# Revit family: Electronics_Visual-TVs_ViewSonic_ViewSonicR-EP4320-5540-5540T-Display
name_source: partatom
category: Electrical Equipment
revit_build: Autodesk Revit 2017 (Build: 20190508_0315(x64)
units: mm (PartAtom-declared; Revit-internal decimal feet)

## family parameters
Always vertical = Yes
Cut with Voids When Loaded = No
OmniClass Number = 23.85.10.14.24.17
OmniClass Title = Plasma Video Monitors
Panel Configuration = Two Columns, Circuits Across
Part Type = Panelboard
Room Calculation Point = No
Round Connector Dimension = Use Diameter
Shared = No
Work Plane-Based = No

## types (3) — shared parameters
Aspect Ratio = 9:16
Assembly Code = D5030500
Backlight = WLED
Contrast Ratio = 1200:1
Cover Material = Plastic - Screen - ViewSonic
Covering Color = Metal - ViewSonic - Black
Edition number = 1
Keynote = 11130
Light Source = DLED
Manufacturer = ViewSonic
Orientation = Portrait
Panel Surface = 7H/ 5mm Tempered glass
Product data url = https://www.bimobject.com
URL = https://www.viewsonic.com
Viewing Angles = H = 178, V = 178 typ.

## per-type parameters (varying)
| type | Backlight Life | Brightness | Colors | Description | Display Area | Display Size | EP4320 | EP5540 | EP5540T | Model | Panel Size | Product Guid | Resolution | Response Time | Screen Material | Surface Treatment | Type/Tech | Viewable Area (In.) |
| EP 4320 | 50,000 hrs | 450 cd/m2 | 16.7M colors | The ViewSonic® EP4320-2 is a 43” all-in-one free-standing digital ePoster kiosk with a sleek, slim design. Great for grabbing attention in busy, high-traffic areas, the EP4320-2 comes with a scratch-proof tempered glass faceplate for added durability. Featuring Full HD 1080p resolution, 178°/178° wide-angle viewing, 450-nit brightness, 1,200:1 contrast ratio, and dual 10W stereo speakers, the EP4320-2 delivers customized multimedia messaging with vivid clarity. Photo and video files can be played back using the embedded Quad-core media player and 16GB of flash storage, or add your own media player using the convenient media player cradle inside the lockable security door. | 43" | 43" | Yes | No | No | viewsonic_ep4320 | 43" | a74ecbe5-cbc1-4ce5-a2fe-00795f225e41 | 1920 x 1080; 16:9 | 14 ms(typ.) | Screen - ePoster - ViewSonic - EP4320 |  |  | 43" |
| EP 5540 | 30,000 Hours Typ. | 350 cd/m2 | 1.07B | The ViewSonic® EP5540 is a 55” 4K Ultra HD all-in-one free-standing digital ePoster kiosk with a sleek, slim design. Great for grabbing attention in busy, high-traffic areas, the EP5540 comes with a scratch-proof tempered glass faceplate for added durability. Featuring an IPS-type panel, 4K Ultra HD resolution, 178°/178° wide-angle viewing, 400-nit brightness, 1,200:1 contrast ratio, and dual 10W stereo speakers, the EP5540 delivers customized multimedia messaging with vivid clarity. Photo and video files can be played back using the embedded Quad-core media player and 16GB of internal memory, or add your own media player using the convenient media player cradle inside the lockable security door. | 1209.6 (H) * 680.4 (V) | 55" | No | Yes | No | viewsonic_ep5540 | 55" | bfec654d-3b3d-45cd-b846-fefad81aa47d | 3840 x 2160; 16:9 | 9 ms (typ. G to G) | Screen - ePoster - ViewSonic - EP5540 | Anti-glare | TFT LCD (IPS type,DLED Backlight) | 55" |
| EP 5540T | 30,000 Hours Typ. | 350 cd/m2 | 1.07B | The ViewSonic® EP5540T is a 10-point interactive, 55” 4K Ultra HD all-in-one free-standing digital ePoster kiosk with a sleek, slim design. Great for grabbing attention in busy, high-traffic areas, the EP5540T comes with a scratch-proof tempered glass faceplate for added durability. Featuring an IPS-type panel, 4K Ultra HD resolution, 178°/178° wide-angle viewing, 400-nit brightness, 1,200:1 contrast ratio, and dual 10W stereo speakers, the EP5540T delivers customized multimedia messaging with vivid clarity. Photo and video files can be played back using the embedded Quad-core media player and 16GB of internal memory, or add your own media player using the convenient media player cradle inside the lockable security door. | 1209.6 (H) * 680.4 (V) | 55" | No | No | Yes | viewsonic_ep5540t | 55" | 701c7aba-dd95-4915-a085-317012c6b0e2 | 3840 x 2160; 16:9 | 9 ms (typ. G to G) | Screen - ePoster - ViewSonic - EP5540T | Anti-glare | TFT LCD (IPS type,DLED Backlight) | 55" |

## geometry (parser evidence)
native form markers: Sweep x10
no freeform markers — native parametric forms only
